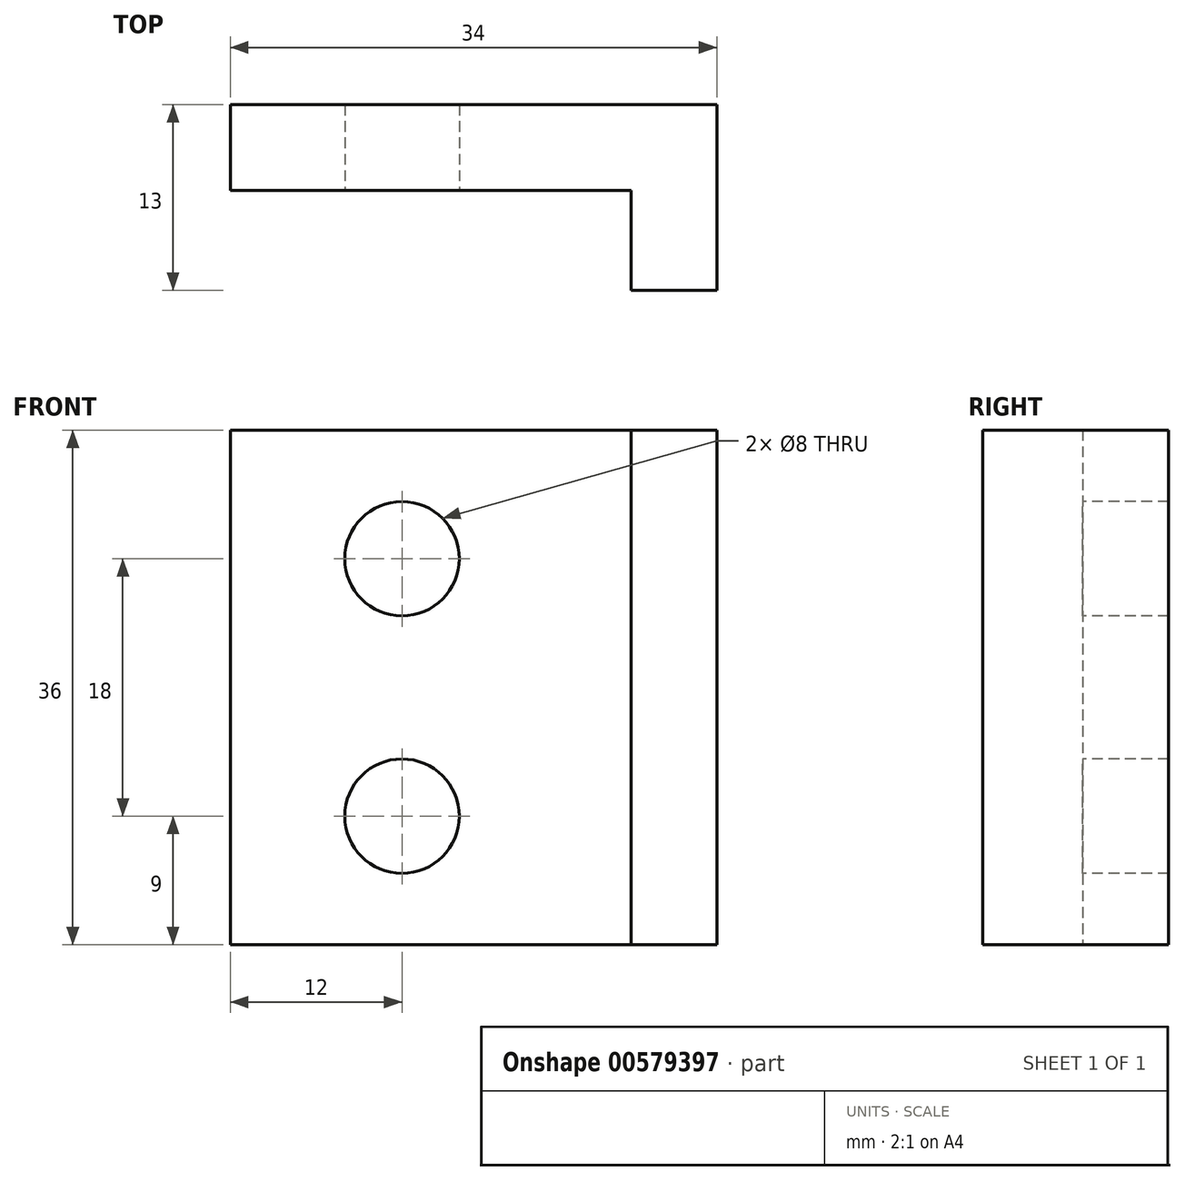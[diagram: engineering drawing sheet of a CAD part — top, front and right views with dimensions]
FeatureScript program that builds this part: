
annotation { "Feature Type Name" : "Feature", "Feature Type Description" : "" }
export const myFeature = defineFeature(function(context is Context, id is Id, definition is map)
    precondition{}
    {
        {
            var Q0;
            Q0=qCreatedBy(makeId("Top.planeOp"),FACE);
            var sketch = newSketch(context, id + "F0", { "sketchPlane" : qUnion([Q0])});
            skLineSegment(sketch, "E0", {"start": v(0, 0) * mm, "end": v(34, 0) * mm});
            skLineSegment(sketch, "E1", {"start": v(34, 0) * mm, "end": v(34, -13) * mm});
            skLineSegment(sketch, "E2", {"start": v(34, -13) * mm, "end": v(28, -13) * mm});
            skLineSegment(sketch, "E3", {"start": v(28, -13) * mm, "end": v(28, -6) * mm});
            skLineSegment(sketch, "E4", {"start": v(28, -6) * mm, "end": v(0, -6) * mm});
            skLineSegment(sketch, "E5", {"start": v(0, -6) * mm, "end": v(0, 0) * mm});
            skSolve(sketch);
        }
        {
            var Q0;
            Q0 = qSketchRegion(id + "F0", true);
            extrude(context, id + "F1", {"entities" : qUnion([Q0]), "depth" : 36 * mm, "offsetDistance" : 25 * mm});
        }
        {
            var Q0;
            Q0=makeQuery(id+"F1.opExtrude","SWEPT_FACE",FACE,{"disambiguationData":[OSD([sQuery(id+"F0.wireOp",EDGE,"E4")])]});
            var sketch = newSketch(context, id + "F2", { "sketchPlane" : qUnion([Q0])});
            skLineSegment(sketch, "E6", {"start": v(12, 34.89) * mm, "end": v(12, 6.06) * mm, "construction": true});
            skCircle(sketch, "E7", {"center": v(12, 27) * mm, "radius": 4 * mm});
            skCircle(sketch, "E8", {"center": v(12, 9) * mm, "radius": 4 * mm});
            skSolve(sketch);
        }
        {
            var Q0;
            Q0 = qSketchRegion(id + "F2", true);
            extrude(context, id + "F3", {"entities" : qUnion([Q0]), "operationType" : NewBodyOperationType.REMOVE, "oppositeDirection" : true, "depth" : 25 * mm, "offsetDistance" : 25 * mm});
        }
    });
